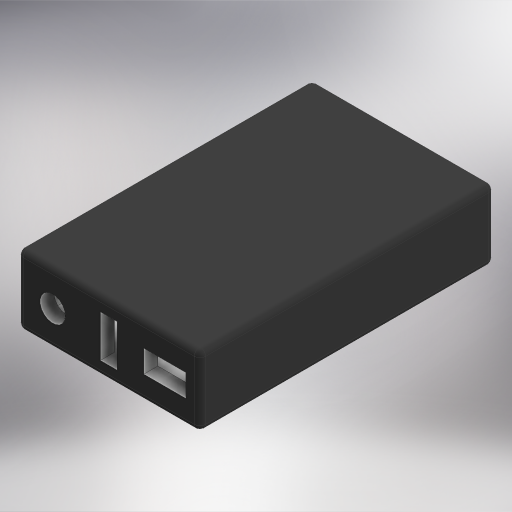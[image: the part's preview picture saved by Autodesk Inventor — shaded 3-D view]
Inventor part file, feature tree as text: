
AUTODESK INVENTOR PART (.ipt)
format: ipt  version: 2024 (Build 280153000, 153)  size: 344,576 bytes
history: native  units: mm
features: other x7, extrude x5, fillet x5, sketch x5, shell x1
ambient origin geometry x8: Origin, YZ Plane, XZ Plane, XY Plane, X Axis, Y Axis, Z Axis, Center Point
bodies: Body1 (feature_tree)
feature tree (23):
  other  "Sólido1"
  extrude  "Extrusión1"  Depth=65.0mm
  shell  "Vaciado1"  Thickness=25.0mm
  extrude  "Extrusión2"  Depth=5.0mm TaperAngle=0.0deg
  extrude  "Extrusión3"  Depth=12.5mm
  extrude  "Extrusión4"  Depth=5.0mm TaperAngle=0.0deg
  extrude  "Extrusión5"  Depth=29.5mm
  fillet  "Empalme6"  Radius=29.5mm
  fillet  "Empalme7"  Radius=5.0mm
  fillet  "Empalme8"  Radius=8.0mm
  fillet  "Empalme9"  Radius=15.0mm
  fillet  "Empalme10"  Radius=8.5mm
  sketch  "Boceto1"  dims[d0=105.0mm d1=65.0mm d2=25.0mm d3=0.0mm]
  sketch  "Boceto2"  dims[d9=5.0mm d10=5.0mm d11=0.0mm]
  sketch  "Boceto3"  dims[d12=9.0mm d13=12.5mm]
  sketch  "Boceto4"  dims[d14=12.5mm d15=5.0mm d16=0.0mm]
  sketch  "Boceto5"  dims[d17=6.0mm d18=29.5mm d19=29.5mm d20=5.0mm d21=0.0mm d22=8.0mm d23=15.0mm d24=8.5mm d25=8.5mm d26=5.0mm d27=5.0mm d28=0.0mm d29=2.0mm d30=2.0mm d31=2.0mm d32=2.0mm d33=2.0mm]
  other  "Finish1"
  other  "Finish2"
  other  "Finish3"
  other  "Finish4"
  other  "Finish5"
  other  "Finish6"
